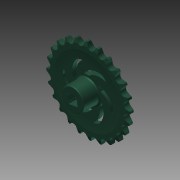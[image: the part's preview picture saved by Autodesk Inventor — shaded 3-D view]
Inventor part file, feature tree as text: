
AUTODESK INVENTOR PART (.ipt)
format: ipt  version: 2013 (Build 170138000, 138)  size: 2,001,408 bytes
history: native  units: mm (DEFAULTED — no unit token found)
features: imported_body x1, sketch x1, other x1, extrude x1
ambient origin geometry x8: Origin, YZ Plane, XZ Plane, XY Plane, X Axis, Y Axis, Z Axis, Center Point
bodies: Solid1 (feature_tree)
feature tree (4):
  imported_body  "Base1"
  sketch  "Sketch1"  dims[d1=2.2606mm d5=25.4mm d6=0.0mm d7=0.0mm d8=0.0mm]
  other  "Srf1"
  extrude  "ExtrusionSrf1"  Depth=25.4mm TaperAngle=0.0deg
